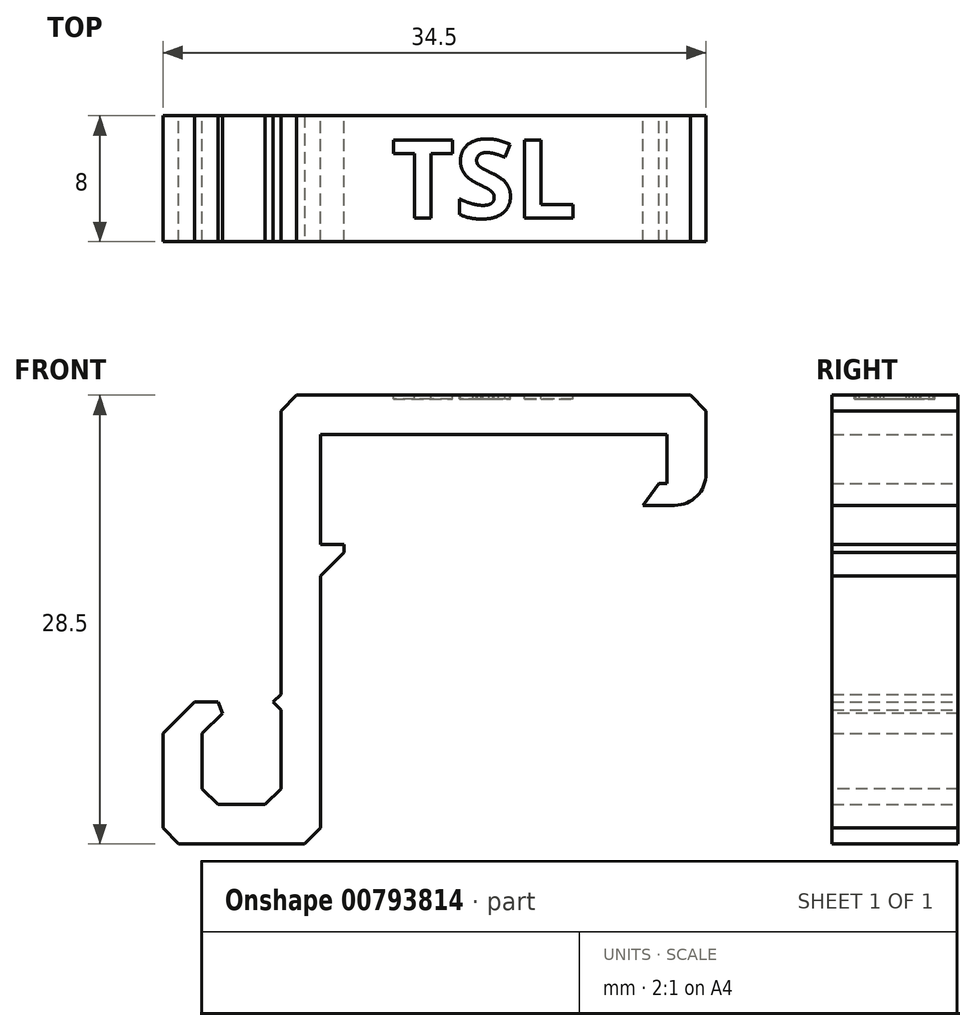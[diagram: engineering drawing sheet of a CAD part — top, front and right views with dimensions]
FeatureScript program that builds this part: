
annotation { "Feature Type Name" : "Feature", "Feature Type Description" : "" }
export const myFeature = defineFeature(function(context is Context, id is Id, definition is map)
    precondition{}
    {
        {
            var Q0;
            Q0=qCreatedBy(makeId("Front.planeOp"),FACE);
            var sketch = newSketch(context, id + "F0", { "sketchPlane" : qUnion([Q0])});
            skLineSegment(sketch, "E0.bottom", {"start": v(0, 0) * mm, "end": v(50, 0) * mm, "construction": true});
            skLineSegment(sketch, "E0.top", {"start": v(0, 25) * mm, "end": v(50, 25) * mm, "construction": true});
            skLineSegment(sketch, "E0.left", {"start": v(0, 0) * mm, "end": v(0, 25) * mm, "construction": true});
            skLineSegment(sketch, "E0.right", {"start": v(50, 0) * mm, "end": v(50, 25) * mm, "construction": true});
            skLineSegment(sketch, "E1.0", {"start": v(50.5, -0.5) * mm, "end": v(50.5, 25.5) * mm, "construction": true});
            skLineSegment(sketch, "E1.1", {"start": v(-0.5, -0.5) * mm, "end": v(50.5, -0.5) * mm, "construction": true});
            skLineSegment(sketch, "E1.2", {"start": v(-0.5, -0.5) * mm, "end": v(-0.5, 16) * mm, "construction": true});
            skLineSegment(sketch, "E1.3", {"start": v(-0.5, 25.5) * mm, "end": v(50.5, 25.5) * mm, "construction": true});
            skLineSegment(sketch, "E2.0", {"start": v(2.6, 22.4) * mm, "end": v(18, 22.4) * mm, "construction": true});
            skLineSegment(sketch, "E2.1", {"start": v(2.6, 2.6) * mm, "end": v(2.6, 22.4) * mm, "construction": true});
            skLineSegment(sketch, "E2.2", {"start": v(2.6, 2.6) * mm, "end": v(45.4, 2.6) * mm, "construction": true});
            skLineSegment(sketch, "E2.3", {"start": v(45.4, 2.6) * mm, "end": v(45.4, 22.4) * mm, "construction": true});
            skLineSegment(sketch, "E3.0", {"start": v(21, 0) * mm, "end": v(21, 25) * mm, "construction": true});
            skLineSegment(sketch, "E4.0", {"start": v(29, 0) * mm, "end": v(29, 25) * mm, "construction": true});
            skLineSegment(sketch, "E5", {"start": v(-0.5, 25.5) * mm, "end": v(-0.5, 18.5) * mm});
            skLineSegment(sketch, "E6", {"start": v(-10.5, -0.5) * mm, "end": v(-10.5, 6.5) * mm});
            skLineSegment(sketch, "E7", {"start": v(-10.5, -0.5) * mm, "end": v(-0.5, -0.5) * mm});
            skLineSegment(sketch, "E8.0", {"start": v(-8, 2) * mm, "end": v(-8, 6.5) * mm});
            skLineSegment(sketch, "E8.1", {"start": v(-8, 2) * mm, "end": v(-3, 2) * mm});
            skLineSegment(sketch, "E8.2", {"start": v(-3, 2) * mm, "end": v(-3, 8) * mm});
            skLineSegment(sketch, "E9", {"start": v(-0.5, 25.5) * mm, "end": v(21.5, 25.5) * mm});
            skLineSegment(sketch, "E10.0", {"start": v(-0.5, 28) * mm, "end": v(21.5, 28) * mm});
            skLineSegment(sketch, "E11", {"start": v(-0.5, 28) * mm, "end": v(-3, 28) * mm});
            skLineSegment(sketch, "E12", {"start": v(-3, 28) * mm, "end": v(-3, 25.5) * mm});
            skLineSegment(sketch, "E13.bottom", {"start": v(21.5, 28) * mm, "end": v(24, 28) * mm});
            skLineSegment(sketch, "E13.left", {"start": v(21.5, 25.5) * mm, "end": v(21.5, 22.4) * mm});
            skLineSegment(sketch, "E13.right", {"start": v(24, 28) * mm, "end": v(24, 22.4) * mm});
            skLineSegment(sketch, "E14.bottom", {"start": v(21.5, 22.4) * mm, "end": v(21, 22.4) * mm});
            skLineSegment(sketch, "E14.top", {"start": v(24, 21) * mm, "end": v(20, 21) * mm});
            skLineSegment(sketch, "E14.left", {"start": v(24, 22.4) * mm, "end": v(24, 21) * mm});
            skLineSegment(sketch, "E15", {"start": v(13.54, 19) * mm, "end": v(-16.95, 19) * mm, "construction": true});
            skLineSegment(sketch, "E16.bottom", {"start": v(-0.5, 18.5) * mm, "end": v(1, 18.5) * mm});
            skLineSegment(sketch, "E16.top", {"start": v(-0.5, 16) * mm, "end": v(1, 16) * mm});
            skLineSegment(sketch, "E16.right", {"start": v(1, 18.5) * mm, "end": v(1, 16) * mm});
            skLineSegment(sketch, "E17.trimOffspring", {"start": v(24, 22.4) * mm, "end": v(45.4, 22.4) * mm, "construction": true});
            skLineSegment(sketch, "E18.trimOffspring", {"start": v(-0.5, 18.5) * mm, "end": v(-0.5, 25.5) * mm, "construction": true});
            skLineSegment(sketch, "E19.trimOffspring", {"start": v(-0.5, 16) * mm, "end": v(-0.5, -0.5) * mm});
            skLineSegment(sketch, "E20", {"start": v(21, 22.4) * mm, "end": v(20, 21) * mm});
            skLineSegment(sketch, "E21.trimOffspring", {"start": v(21, 22.4) * mm, "end": v(21.5, 22.4) * mm, "construction": true});
            skLineSegment(sketch, "E22", {"start": v(-10.5, 6.5) * mm, "end": v(-8.5, 8.5) * mm});
            skLineSegment(sketch, "E23", {"start": v(-8, 6.5) * mm, "end": v(-6, 8.5) * mm});
            skLineSegment(sketch, "E24", {"start": v(-8.5, 8.5) * mm, "end": v(-6, 8.5) * mm});
            skLineSegment(sketch, "E25", {"start": v(-3.5, 8.5) * mm, "end": v(-3, 9) * mm});
            skLineSegment(sketch, "E26", {"start": v(-3.5, 8.5) * mm, "end": v(-3, 8) * mm});
            skLineSegment(sketch, "E27.trimOffspring", {"start": v(-3, 9) * mm, "end": v(-3, 25.5) * mm});
            skSolve(sketch);
        }
        {
            var Q0;
            Q0=makeQuery(id+"F0.imprint","IMPRINT",FACE,{"disambiguationData":[TD([[makeQuery(id+"F0.imprint","IMPRINT",EDGE,{"derivedFrom":sQuery(id+"F0.wireOp",EDGE,"E5")}),-1.0]])]});
            extrude(context, id + "F1", {"entities" : qUnion([Q0]), "depth" : 8 * mm, "offsetDistance" : 25 * mm});
        }
        {
            var Q0;
            Q0=makeQuery(id+"F1.opExtrude","SWEPT_EDGE",EDGE,{"disambiguationData":[OSD([sQuery(id+"F0.wireOp",EDGE,"E16.top"),sQuery(id+"F0.wireOp",EDGE,"E16.right")])]});
            chamfer(context, id + "F2", {"entities" : qUnion([Q0]), "width" : 2 * mm, "tangentPropagation" : true});
        }
        {
            var Q0;
            {var subQ0=sQuery(id+"F0.wireOp",EDGE,"E14.top");Q0=makeQuery(id+"F2.opChamfer","BLEND_EDGE",EDGE,{"blendedFrom":[makeQuery(id+"F1.opExtrude","SWEPT_EDGE",EDGE,{"disambiguationData":[OSD([subQ0,sQuery(id+"F0.wireOp",EDGE,"E14.right")])]}),makeQuery(id+"F1.opExtrude","SWEPT_FACE",FACE,{"disambiguationData":[OSD([subQ0])]})],"blendedInto":[makeQuery(id+"F1.opExtrude","SWEPT_FACE",FACE,{"disambiguationData":[OSD([subQ0])]})]});}
            var Q1;
            Q1=makeQuery(id+"F1.opExtrude","SWEPT_EDGE",EDGE,{"disambiguationData":[OSD([sQuery(id+"F0.wireOp",EDGE,"E14.top"),sQuery(id+"F0.wireOp",EDGE,"E14.left")])]});
            fillet(context, id + "F3", {"entities" : qUnion([Q0, Q1]), "radius" : 2 * mm, "tangentPropagation" : true, "allowEdgeOverflow" : false});
        }
        {
            var Q0;
            Q0=makeQuery(id+"F1.opExtrude","SWEPT_EDGE",EDGE,{"disambiguationData":[OSD([sQuery(id+"F0.wireOp",EDGE,"E7"),sQuery(id+"F0.wireOp",EDGE,"E19.trimOffspring")])]});
            var Q1;
            Q1=makeQuery(id+"F1.opExtrude","SWEPT_EDGE",EDGE,{"disambiguationData":[OSD([sQuery(id+"F0.wireOp",EDGE,"E8.1"),sQuery(id+"F0.wireOp",EDGE,"E8.2")])]});
            var Q2;
            Q2=makeQuery(id+"F1.opExtrude","SWEPT_EDGE",EDGE,{"disambiguationData":[OSD([sQuery(id+"F0.wireOp",EDGE,"E13.bottom"),sQuery(id+"F0.wireOp",EDGE,"E13.right")])]});
            var Q3;
            Q3=makeQuery(id+"F1.opExtrude","SWEPT_EDGE",EDGE,{"disambiguationData":[OSD([sQuery(id+"F0.wireOp",EDGE,"E11"),sQuery(id+"F0.wireOp",EDGE,"E12")])]});
            var Q4;
            Q4=makeQuery(id+"F1.opExtrude","SWEPT_EDGE",EDGE,{"disambiguationData":[OSD([sQuery(id+"F0.wireOp",EDGE,"E8.0"),sQuery(id+"F0.wireOp",EDGE,"E8.1")])]});
            var Q5;
            Q5=makeQuery(id+"F1.opExtrude","SWEPT_EDGE",EDGE,{"disambiguationData":[OSD([sQuery(id+"F0.wireOp",EDGE,"E6"),sQuery(id+"F0.wireOp",EDGE,"E7")])]});
            chamfer(context, id + "F4", {"entities" : qUnion([Q0, Q1, Q2, Q3, Q4, Q5]), "width" : 1 * mm, "tangentPropagation" : true});
        }
        {
            var Q0;
            Q0=makeQuery(id+"F1.opExtrude","SWEPT_FACE",FACE,{"disambiguationData":[OSD([sQuery(id+"F0.wireOp",EDGE,"E10.0"),sQuery(id+"F0.wireOp",EDGE,"E11"),sQuery(id+"F0.wireOp",EDGE,"E13.bottom")])]});
            var sketch = newSketch(context, id + "F5", { "sketchPlane" : qUnion([Q0])});
            skText(sketch, "E28", { "text": "TSL", "fontName": "OpenSans-Bold.ttf"});
            const initialGuessF5  = {"E28": [0.004, -0.0065, 1, 0, 0.005]};
            skSetInitialGuess(sketch, initialGuessF5);
            skSolve(sketch);
        }
        {
            var Q0;
            Q0=makeQuery(id+"F5.imprint","IMPRINT",FACE,{"disambiguationData":[TD([[makeQuery(id+"F5.imprint","IMPRINT",EDGE,{"derivedFrom":sQuery(id+"F5.wireOp",EDGE,"E28.sketch_text.stroke-0")}),-1.0]])]});
            var Q1;
            Q1=makeQuery(id+"F5.imprint","IMPRINT",FACE,{"disambiguationData":[TD([[makeQuery(id+"F5.imprint","IMPRINT",EDGE,{"derivedFrom":sQuery(id+"F5.wireOp",EDGE,"E28.sketch_text.stroke-8")}),-1.0]])]});
            var Q2;
            Q2=makeQuery(id+"F5.imprint","IMPRINT",FACE,{"disambiguationData":[TD([[makeQuery(id+"F5.imprint","IMPRINT",EDGE,{"derivedFrom":sQuery(id+"F5.wireOp",EDGE,"E28.sketch_text.stroke-36")}),-1.0]])]});
            extrude(context, id + "F6", {"entities" : qUnion([Q0, Q1, Q2]), "operationType" : NewBodyOperationType.REMOVE, "oppositeDirection" : true, "depth" : 0.25 * mm, "offsetDistance" : 25 * mm});
        }
        {
            var Q0;
            Q0=makeQuery(id+"F1.opExtrude","SWEPT_EDGE",EDGE,{"disambiguationData":[OSD([sQuery(id+"F0.wireOp",EDGE,"E23"),sQuery(id+"F0.wireOp",EDGE,"E24")])]});
            chamfer(context, id + "F7", {"entities" : qUnion([Q0]), "width" : 1 * mm, "tangentPropagation" : true});
        }
    });
